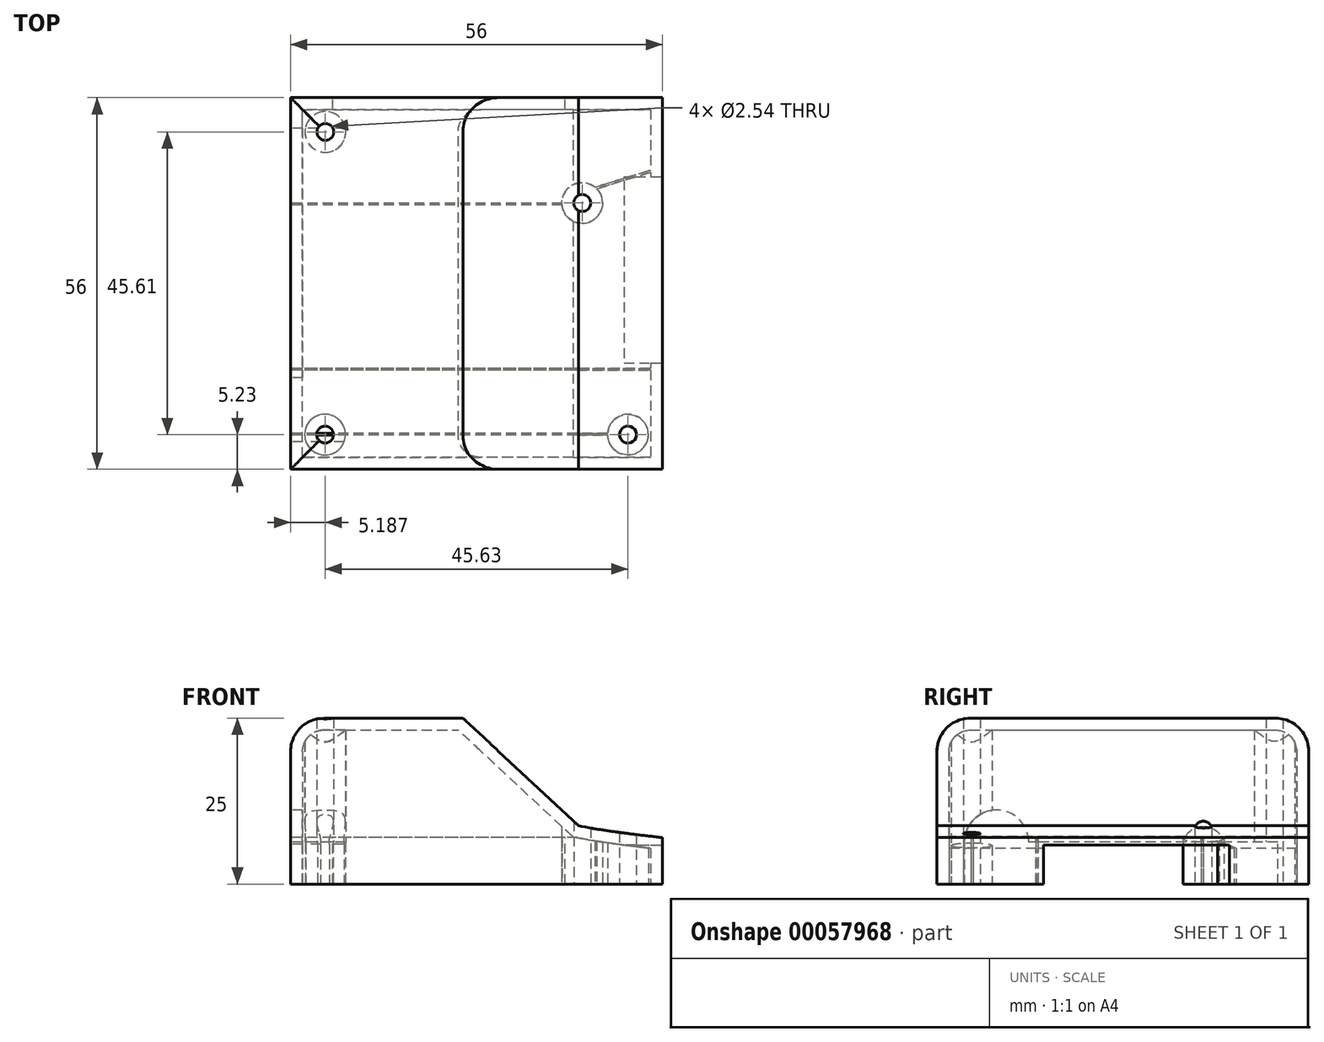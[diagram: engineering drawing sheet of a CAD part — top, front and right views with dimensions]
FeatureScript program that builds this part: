
annotation { "Feature Type Name" : "Feature", "Feature Type Description" : "" }
export const myFeature = defineFeature(function(context is Context, id is Id, definition is map)
    precondition{}
    {
        {
            var Q0;
            Q0=qCreatedBy(makeId("Top.planeOp"),FACE);
            var sketch = newSketch(context, id + "F0", { "sketchPlane" : qUnion([Q0])});
            skLineSegment(sketch, "E0.rect.bottom", {"start": v(22.84, -21.13) * mm, "end": v(-26.83, -21.13) * mm});
            skLineSegment(sketch, "E0.rect.top", {"start": v(22.84, 28.7) * mm, "end": v(-26.83, 28.7) * mm});
            skLineSegment(sketch, "E0.rect.left", {"start": v(22.84, -21.13) * mm, "end": v(22.84, 28.7) * mm});
            skPoint(sketch, "E0.rect.middle", {"position": v(-2, 3.78) * mm});
            skCircle(sketch, "E1", {"center": v(-24.81, -18.99) * mm, "radius": 1.27 * mm});
            skCircle(sketch, "E2", {"center": v(-24.76, 26.62) * mm, "radius": 1.27 * mm});
            skCircle(sketch, "E3", {"center": v(13.92, 15.91) * mm, "radius": 1.27 * mm});
            skLineSegment(sketch, "E4", {"start": v(-2, -21.13) * mm, "end": v(-2, -18.21) * mm});
            skCircle(sketch, "E5.MirrorC", {"center": v(20.82, -18.99) * mm, "radius": 1.27 * mm});
            skLineSegment(sketch, "E6.rect.bottom", {"start": v(24.75, -22.97) * mm, "end": v(-28.75, -22.97) * mm});
            skLineSegment(sketch, "E6.rect.top", {"start": v(24.75, 30.53) * mm, "end": v(-28.75, 30.53) * mm});
            skLineSegment(sketch, "E6.rect.left", {"start": v(24.75, -22.97) * mm, "end": v(24.75, 30.53) * mm});
            skLineSegment(sketch, "E6.rect.right", {"start": v(-28.75, -22.97) * mm, "end": v(-28.75, 30.53) * mm});
            skLineSegment(sketch, "E7.rect.bottom", {"start": v(26, -24.22) * mm, "end": v(-30, -24.22) * mm});
            skLineSegment(sketch, "E7.rect.top", {"start": v(26, 31.78) * mm, "end": v(-30, 31.78) * mm});
            skLineSegment(sketch, "E7.rect.left", {"start": v(26, -24.22) * mm, "end": v(26, 31.78) * mm});
            skLineSegment(sketch, "E7.rect.right", {"start": v(-30, -24.22) * mm, "end": v(-30, 31.78) * mm});
            skPoint(sketch, "E8", {"position": v(8.65, 14) * mm});
            skSolve(sketch);
        }
        {
            var Q0;
            Q0=qSketchRegion(id+"F0",true);
            var Q1;
            Q1=makeQuery(id+"F0.imprint","IMPRINT",FACE,{"disambiguationData":[TD([[makeQuery(id+"F0.imprint","IMPRINT",EDGE,{"derivedFrom":sQuery(id+"F0.wireOp",EDGE,"E1")}),-1.0]])]});
            extrude(context, id + "F1", {"entities" : qUnion([Q0, Q1]), "depth" : 25 * mm});
        }
        {
            var Q0;
            Q0=qCreatedBy(makeId("Front.planeOp"),FACE);
            var sketch = newSketch(context, id + "F2", { "sketchPlane" : qUnion([Q0])});
            skLineSegment(sketch, "E9", {"start": v(0, 0) * mm, "end": v(0, 7) * mm});
            skLineSegment(sketch, "E10", {"start": v(0, 7) * mm, "end": v(26.03, 7) * mm});
            skFitSpline(sketch, "E11", {"points": [v(26.03, 7) * mm, v(0, 12.35) * mm, v(-16.78, 25.51) * mm], "startDerivative": vector(-52.99, 5.48) * mm, "endDerivative": vector(-32.25, 32.04) * mm});
            skLineSegment(sketch, "E12", {"start": v(26.03, 7) * mm, "end": v(26.03, 25.51) * mm});
            skLineSegment(sketch, "E13", {"start": v(26.03, 25.51) * mm, "end": v(-16.78, 25.51) * mm});
            skFitSpline(sketch, "E14", {"points": [v(26.03, 7) * mm, v(6, 12.87) * mm, v(0, 25.51) * mm], "startDerivative": vector(-42.79, 5.9) * mm, "endDerivative": vector(-8.1, 32) * mm});
            skFitSpline(sketch, "E15", {"points": [v(26.03, 7) * mm, v(2.41, 13.05) * mm, v(-4.6, 25.51) * mm], "startDerivative": vector(-48.93, 5.58) * mm, "endDerivative": vector(-10.6, 32.65) * mm});
            skLineSegment(sketch, "E16", {"start": v(-4.6, 25.51) * mm, "end": v(15.3, 7) * mm});
            skLineSegment(sketch, "E17", {"start": v(15.3, 7) * mm, "end": v(26.03, 7) * mm});
            skSolve(sketch);
        }
        {
            var Q0;
            {var subQ0=sQuery(id+"F2.wireOp",EDGE,"E14");Q0=makeQuery(id+"F2.imprint","IMPRINT",FACE,{"disambiguationData":[TD([[makeQuery(id+"F2.imprint","IMPRINT",EDGE,{"derivedFrom":subQ0}),1.0]])]});}
            var Q1;
            {var subQ0=sQuery(id+"F2.wireOp",EDGE,"E12");Q1=makeQuery(id+"F2.imprint","IMPRINT",FACE,{"disambiguationData":[TD([[makeQuery(id+"F2.imprint","IMPRINT",EDGE,{"derivedFrom":subQ0}),1.0]])]});}
            extrude(context, id + "F3", {"entities" : qUnion([Q0, Q1]), "operationType" : NewBodyOperationType.REMOVE, "endBound" : BoundingType.UP_TO_NEXT, "oppositeDirection" : true, "depth" : 25 * mm, "hasSecondDirection" : true, "secondDirectionOppositeDirection" : false, "secondDirectionDepth" : 25 * mm});
        }
        {
            var Q0;
            Q0=makeQuery(id+"F1.opExtrude","CAP_EDGE",EDGE,{"disambiguationData":[OSD([sQuery(id+"F0.wireOp",EDGE,"E7.rect.right")])],"isStart":false});
            var Q1;
            Q1=makeQuery(id+"F3.boolean.opBoolean","COPY",EDGE,{"derivedFrom":makeQuery(id+"F3.opExtrude","TWEAK_EDGE",EDGE,{"derivedFrom":[makeQuery(id+"F1.opExtrude","CAP_FACE",FACE,{"disambiguationData":[OSD([sQuery(id+"F0.wireOp",EDGE,"E1"),sQuery(id+"F0.wireOp",EDGE,"E2"),sQuery(id+"F0.wireOp",EDGE,"E3"),sQuery(id+"F0.wireOp",EDGE,"E5.MirrorC"),sQuery(id+"F0.wireOp",EDGE,"E7.rect.bottom"),sQuery(id+"F0.wireOp",EDGE,"E7.rect.top"),sQuery(id+"F0.wireOp",EDGE,"E7.rect.left"),sQuery(id+"F0.wireOp",EDGE,"E7.rect.right")])],"isStart":false}),makeQuery(id+"F2.imprint","IMPRINT",EDGE,{"derivedFrom":sQuery(id+"F2.wireOp",EDGE,"E11")})]})});
            var Q2;
            Q2=makeQuery(id+"F3.boolean.opBoolean","COPY",EDGE,{"derivedFrom":makeQuery(id+"F3.opExtrude","TWEAK_EDGE",EDGE,{"derivedFrom":[makeQuery(id+"F1.opExtrude","CAP_FACE",FACE,{"disambiguationData":[OSD([sQuery(id+"F0.wireOp",EDGE,"E1"),sQuery(id+"F0.wireOp",EDGE,"E2"),sQuery(id+"F0.wireOp",EDGE,"E3"),sQuery(id+"F0.wireOp",EDGE,"E5.MirrorC"),sQuery(id+"F0.wireOp",EDGE,"E7.rect.bottom"),sQuery(id+"F0.wireOp",EDGE,"E7.rect.top"),sQuery(id+"F0.wireOp",EDGE,"E7.rect.left"),sQuery(id+"F0.wireOp",EDGE,"E7.rect.right")])],"isStart":false}),makeQuery(id+"F2.imprint","IMPRINT",EDGE,{"derivedFrom":sQuery(id+"F2.wireOp",EDGE,"E15")})]})});
            var Q3;
            Q3=makeQuery(id+"F3.boolean.opBoolean","COPY",EDGE,{"derivedFrom":makeQuery(id+"F3.opExtrude","CAP_EDGE",EDGE,{"disambiguationData":[OSD([sQuery(id+"F2.wireOp",EDGE,"E16")]),topologyDisambiguationEdgeConnected([makeQuery(id+"F1.opExtrude","CAP_FACE",FACE,{"disambiguationData":[OSD([sQuery(id+"F0.wireOp",EDGE,"E1"),sQuery(id+"F0.wireOp",EDGE,"E2"),sQuery(id+"F0.wireOp",EDGE,"E3"),sQuery(id+"F0.wireOp",EDGE,"E5.MirrorC"),sQuery(id+"F0.wireOp",EDGE,"E7.rect.bottom"),sQuery(id+"F0.wireOp",EDGE,"E7.rect.top"),sQuery(id+"F0.wireOp",EDGE,"E7.rect.left"),sQuery(id+"F0.wireOp",EDGE,"E7.rect.right")])],"isStart":false})])],"isStart":false})});
            var Q4;
            {var subQ0=sQuery(id+"F2.wireOp",EDGE,"E16");var subQ1=sQuery(id+"F2.wireOp",EDGE,"E14");var subQ2=makeQuery(id+"F2.imprint","INTERSECT",VERTEX,{"disambiguationData":[OD(0.0)],"derivedFrom":[subQ1,subQ0]});var subQ3=sQuery(id+"F2.wireOp",EDGE,"E15");var subQ4=makeQuery(id+"F2.imprint","INTERSECT",VERTEX,{"derivedFrom":[subQ3,subQ0]});var subQ5=makeQuery(id+"F2.imprint","INTERSECT",VERTEX,{"disambiguationData":[OD(1.0)],"derivedFrom":[subQ1,subQ0]});Q4=makeQuery(id+"F3.boolean.opBoolean","COPY",EDGE,{"derivedFrom":makeQuery(id+"F3.opExtrude","TWEAK_EDGE",EDGE,{"disambiguationData":[OD(0.0)],"derivedFrom":[makeQuery(id+"F2.imprint","IMPRINT",EDGE,{"disambiguationData":[TD([[subQ4,1.0]])],"derivedFrom":subQ3}),makeQuery(id+"F2.imprint","IMPRINT",EDGE,{"disambiguationData":[TD([[subQ5,1.0]])],"derivedFrom":subQ0}),makeQuery(id+"F2.imprint","IMPRINT",EDGE,{"disambiguationData":[TD([[subQ2,1.0]])],"derivedFrom":subQ0}),makeQuery(id+"F2.imprint","IMPRINT",EDGE,{"disambiguationData":[TD([[subQ2,-1.0]])],"derivedFrom":subQ0})]})});}
            var Q5;
            {var subQ0=sQuery(id+"F2.wireOp",EDGE,"E16");var subQ1=sQuery(id+"F2.wireOp",EDGE,"E14");var subQ2=makeQuery(id+"F2.imprint","INTERSECT",VERTEX,{"disambiguationData":[OD(0.0)],"derivedFrom":[subQ1,subQ0]});var subQ3=sQuery(id+"F2.wireOp",EDGE,"E15");var subQ4=makeQuery(id+"F2.imprint","INTERSECT",VERTEX,{"derivedFrom":[subQ3,subQ0]});var subQ5=makeQuery(id+"F2.imprint","INTERSECT",VERTEX,{"disambiguationData":[OD(1.0)],"derivedFrom":[subQ1,subQ0]});Q5=makeQuery(id+"F3.boolean.opBoolean","COPY",EDGE,{"derivedFrom":makeQuery(id+"F3.opExtrude","TWEAK_EDGE",EDGE,{"disambiguationData":[OD(1.0)],"derivedFrom":[makeQuery(id+"F2.imprint","IMPRINT",EDGE,{"disambiguationData":[TD([[subQ4,1.0]])],"derivedFrom":subQ3}),makeQuery(id+"F2.imprint","IMPRINT",EDGE,{"disambiguationData":[TD([[subQ5,1.0]])],"derivedFrom":subQ0}),makeQuery(id+"F2.imprint","IMPRINT",EDGE,{"disambiguationData":[TD([[subQ2,1.0]])],"derivedFrom":subQ0}),makeQuery(id+"F2.imprint","IMPRINT",EDGE,{"disambiguationData":[TD([[subQ2,-1.0]])],"derivedFrom":subQ0})]})});}
            var Q6;
            Q6=makeQuery(id+"F1.opExtrude","CAP_EDGE",EDGE,{"disambiguationData":[OSD([sQuery(id+"F0.wireOp",EDGE,"E7.rect.bottom")])],"isStart":false});
            var Q7;
            Q7=makeQuery(id+"F3.boolean.opBoolean","COPY",EDGE,{"derivedFrom":makeQuery(id+"F3.opExtrude","CAP_EDGE",EDGE,{"disambiguationData":[OSD([sQuery(id+"F2.wireOp",EDGE,"E16")])],"isStart":true})});
            var Q8;
            Q8=makeQuery(id+"F1.opExtrude","CAP_EDGE",EDGE,{"disambiguationData":[OSD([sQuery(id+"F0.wireOp",EDGE,"E7.rect.top")])],"isStart":false});
            var Q9;
            Q9=makeQuery(id+"F3.boolean.opBoolean","COPY",EDGE,{"derivedFrom":makeQuery(id+"F3.opExtrude","CAP_EDGE",EDGE,{"disambiguationData":[OSD([sQuery(id+"F2.wireOp",EDGE,"E16")]),topologyDisambiguationEdgeConnected([makeQuery(id+"F1.opExtrude","SWEPT_FACE",FACE,{"disambiguationData":[OSD([sQuery(id+"F0.wireOp",EDGE,"E7.rect.top")])]})])],"isStart":false})});
            fillet(context, id + "F4", {"entities" : qUnion([Q0, Q1, Q2, Q3, Q4, Q5, Q6, Q7, Q8, Q9]), "radius" : 5 * mm, "tangentPropagation" : true, "allowEdgeOverflow" : false});
        }
        {
            var Q0;
            Q0=makeQuery(id+"F1.opExtrude","SWEPT_BODY",BODY,{"disambiguationData":[OSD([sQuery(id+"F0.wireOp",EDGE,"E1"),sQuery(id+"F0.wireOp",EDGE,"E2"),sQuery(id+"F0.wireOp",EDGE,"E3"),sQuery(id+"F0.wireOp",EDGE,"E5.MirrorC"),sQuery(id+"F0.wireOp",EDGE,"E7.rect.bottom"),sQuery(id+"F0.wireOp",EDGE,"E7.rect.top"),sQuery(id+"F0.wireOp",EDGE,"E7.rect.left"),sQuery(id+"F0.wireOp",EDGE,"E7.rect.right")])]});
            transform(context, id + "F5", {"entities" : qUnion([Q0]), "transformType" : TransformType.TRANSLATION_3D, "dx" : -5 * mm, "dy" : -12 * mm, "dz" : 0 * mm, "makeCopy" : false});
        }
        {
            var Q0;
            Q0=makeQuery(id+"F1.opExtrude","CAP_FACE",FACE,{"disambiguationData":[OSD([sQuery(id+"F0.wireOp",EDGE,"E1"),sQuery(id+"F0.wireOp",EDGE,"E2"),sQuery(id+"F0.wireOp",EDGE,"E3"),sQuery(id+"F0.wireOp",EDGE,"E5.MirrorC"),sQuery(id+"F0.wireOp",EDGE,"E7.rect.bottom"),sQuery(id+"F0.wireOp",EDGE,"E7.rect.top"),sQuery(id+"F0.wireOp",EDGE,"E7.rect.left"),sQuery(id+"F0.wireOp",EDGE,"E7.rect.right")])],"isStart":true});
            shell(context, id + "F6", {"entities" : qUnion([Q0]), "thickness" : 1.8 * mm});
        }
        {
            var Q0;
            Q0=makeQuery(id+"F1.opExtrude","SWEPT_FACE",FACE,{"disambiguationData":[OSD([sQuery(id+"F0.wireOp",EDGE,"E7.rect.left")])]});
            cPlane(context, id + "F7", {"entities" : qUnion([Q0]), "cplaneType" : CPlaneType.OFFSET, "offset" : 0 * mm, "width" : 150 * mm, "height" : 150 * mm});
        }
        {
            var Q0;
            Q0=qCreatedBy(id+"F7.planeOp",FACE);
            var sketch = newSketch(context, id + "F8", { "sketchPlane" : qUnion([Q0])});
            skLineSegment(sketch, "E18.bottom", {"start": v(7.84, 0) * mm, "end": v(-20.2, 0) * mm});
            skLineSegment(sketch, "E18.top", {"start": v(7.84, 5.87) * mm, "end": v(-20.2, 5.87) * mm});
            skLineSegment(sketch, "E18.left", {"start": v(7.84, 0) * mm, "end": v(7.84, 5.87) * mm});
            skLineSegment(sketch, "E18.right", {"start": v(-20.2, 0) * mm, "end": v(-20.2, 5.87) * mm});
            skSolve(sketch);
        }
        {
            var Q0;
            Q0=qSketchRegion(id+"F8",true);
            extrude(context, id + "F9", {"entities" : qUnion([Q0]), "operationType" : NewBodyOperationType.REMOVE, "endBound" : BoundingType.UP_TO_NEXT, "oppositeDirection" : true, "depth" : 25 * mm});
        }
        {
            var Q0;
            Q0=makeQuery(id+"F1.opExtrude","SWEPT_FACE",FACE,{"disambiguationData":[OSD([sQuery(id+"F0.wireOp",EDGE,"E7.rect.right")])]});
            cPlane(context, id + "F10", {"entities" : qUnion([Q0]), "cplaneType" : CPlaneType.OFFSET, "offset" : 0 * mm, "width" : 150 * mm, "height" : 150 * mm});
        }
        {
            var Q0;
            Q0=qCreatedBy(id+"F10.planeOp",FACE);
            var sketch = newSketch(context, id + "F11", { "sketchPlane" : qUnion([Q0])});
            skLineSegment(sketch, "E19.bottom", {"start": v(-15.15, 0) * mm, "end": v(22.4, 0) * mm});
            skLineSegment(sketch, "E19.top", {"start": v(-15.15, 6.31) * mm, "end": v(22.4, 6.31) * mm});
            skLineSegment(sketch, "E19.left", {"start": v(-15.15, 0) * mm, "end": v(-15.15, 6.31) * mm});
            skArc(sketch, "E20", {"start": v(32.08, 6) * mm, "mid": v(27.4, 11.15) * mm, "end": v(22.4, 6.31) * mm});
            skLineSegment(sketch, "E21", {"start": v(32.08, 6.63) * mm, "end": v(32.08, 0) * mm});
            skLineSegment(sketch, "E22", {"start": v(32.08, 0) * mm, "end": v(22.4, 0) * mm});
            skSolve(sketch);
        }
        {
            var Q0;
            Q0=qSketchRegion(id+"F11",true);
            extrude(context, id + "F12", {"entities" : qUnion([Q0]), "operationType" : NewBodyOperationType.REMOVE, "oppositeDirection" : true, "depth" : 25 * mm});
        }
        {
            var Q0;
            Q0=makeQuery(id+"F1.opExtrude","SWEPT_FACE",FACE,{"disambiguationData":[OSD([sQuery(id+"F0.wireOp",EDGE,"E7.rect.top")])]});
            cPlane(context, id + "F13", {"entities" : qUnion([Q0]), "cplaneType" : CPlaneType.OFFSET, "offset" : 0 * mm, "width" : 150 * mm, "height" : 150 * mm});
        }
        {
            var Q0;
            Q0=qCreatedBy(id+"F13.planeOp",FACE);
            var sketch = newSketch(context, id + "F14", { "sketchPlane" : qUnion([Q0])});
            skLineSegment(sketch, "E23.bottom", {"start": v(-6.36, 0) * mm, "end": v(28.67, 0) * mm});
            skLineSegment(sketch, "E23.top", {"start": v(-6.36, 7.05) * mm, "end": v(28.67, 7.05) * mm});
            skLineSegment(sketch, "E23.left", {"start": v(-6.36, 0) * mm, "end": v(-6.36, 7.05) * mm});
            skLineSegment(sketch, "E23.right", {"start": v(28.67, 0) * mm, "end": v(28.67, 7.05) * mm});
            skSolve(sketch);
        }
        {
            var Q0;
            Q0=qSketchRegion(id+"F14",true);
            extrude(context, id + "F15", {"entities" : qUnion([Q0]), "operationType" : NewBodyOperationType.REMOVE, "endBound" : BoundingType.UP_TO_NEXT, "oppositeDirection" : true, "depth" : 25 * mm});
        }
        {
            var Q0;
            Q0=qCreatedBy(makeId("Top.planeOp"),FACE);
            var sketch = newSketch(context, id + "F16", { "sketchPlane" : qUnion([Q0])});
            skLineSegment(sketch, "E24", {"start": v(12.81, -31.08) * mm, "end": v(12.81, -30.78) * mm});
            skLineSegment(sketch, "E25", {"start": v(19.24, -20.99) * mm, "end": v(19.24, -21.29) * mm});
            skLineSegment(sketch, "E26", {"start": v(19.24, 8.54) * mm, "end": v(19.24, 8.84) * mm});
            skLineSegment(sketch, "E27", {"start": v(5.94, 3.59) * mm, "end": v(5.94, 3.89) * mm});
            skLineSegment(sketch, "E28", {"start": v(10.65, 6.22) * mm, "end": v(10.65, 5.92) * mm});
            skLineSegment(sketch, "E29", {"start": v(10.65, 6.22) * mm, "end": v(19.24, 8.84) * mm});
            skLineSegment(sketch, "E30", {"start": v(10.65, 5.92) * mm, "end": v(19.24, 8.54) * mm});
            skLineSegment(sketch, "E31", {"start": v(19.24, -21.29) * mm, "end": v(-34.98, -21.29) * mm});
            skLineSegment(sketch, "E32", {"start": v(19.24, -20.99) * mm, "end": v(-34.98, -20.99) * mm});
            skLineSegment(sketch, "E33", {"start": v(-34.98, -20.99) * mm, "end": v(-34.98, -21.29) * mm});
            skLineSegment(sketch, "E34", {"start": v(12.81, -31.08) * mm, "end": v(-34.98, -31.08) * mm});
            skLineSegment(sketch, "E35", {"start": v(12.81, -30.78) * mm, "end": v(-34.98, -30.78) * mm});
            skLineSegment(sketch, "E36", {"start": v(-34.98, -30.78) * mm, "end": v(-34.98, -31.08) * mm});
            skLineSegment(sketch, "E37", {"start": v(5.94, 3.59) * mm, "end": v(-34.95, 3.59) * mm});
            skLineSegment(sketch, "E38", {"start": v(5.94, 3.89) * mm, "end": v(-34.95, 3.89) * mm});
            skLineSegment(sketch, "E39", {"start": v(-34.95, 3.89) * mm, "end": v(-34.95, 3.59) * mm});
            skSolve(sketch);
        }
        {
            var Q0;
            Q0=qSketchRegion(id+"F16",true);
            extrude(context, id + "F17", {"entities" : qUnion([Q0]), "operationType" : NewBodyOperationType.ADD, "depth" : 7 * mm});
        }
    });
